# Revit family: Toilet_Tissue_Dispenser-Bobrick-B-540_Series
name_source: partatom
category: Plumbing Fixtures
revit_build: Autodesk Revit 2016 (Build: 20150714_1515(x64)
units: mm (PartAtom-declared; Revit-internal decimal feet)

## family parameters
Cut with Voids When Loaded = No
Host = Face
OmniClass Number = 23.40.20.21.21
OmniClass Title = Toilet Paper Dispensers
Part Type = Normal
Room Calculation Point = No
Round Connector Dimension = Use Diameter
Shared = Yes

## types (1)
- B-540
    ATS URL = http://www.atsspec.net
    Assembly Code = E1090900
    CW Connection = No
    CWFU = 0
    Default Elevation = 22"
    Description = Bobrick Surface-Mounted Toilet Tissue Dispenser & Utility Shelf
    HW Connection = No
    HWFU = 0
    Height = 3 3/4"
    Installation Type = Surface Mounted
    Length = 3 3/4"
    Manufacturer = Bobrick
    Material = Stainless Steel-Bobrick-Type 304-Polished
    Model = B-540
    Omniclass Table 23 Code = 23.40.20.21.21
    Omniclass Table 23 Title = Toilet Paper Dispensers
    Price = Prices may vary. Please consult Manufacturer Representative for most up-to-date price list.
    Product Documentation Link = https://www.bobrick.com
    Product Page URL = https://www.bobrick.com
    Specification = Surface-mounted dual-roll toilet tissue dispenser shall be type-304 stainless steel with bright polished finish. Shell and flange shall be 22 gauge (6.8mm) and have drawn, one-piece, seamless construction. Unit shall be equipped with 18-gauge (1.2mm) hoods hinged to shell. *Spindles shall be chrome-plated plastic with heavy-duty internal springs.
    URL = http://www.bobrick.com
    Vent Connection = No
    WFU = 0
    Warranty Information = 1 Year Limited Warranty
    Waste Connection = No
    Width = 11"

## geometry (parser evidence)
native form markers: Sweep x3
no freeform markers — native parametric forms only
